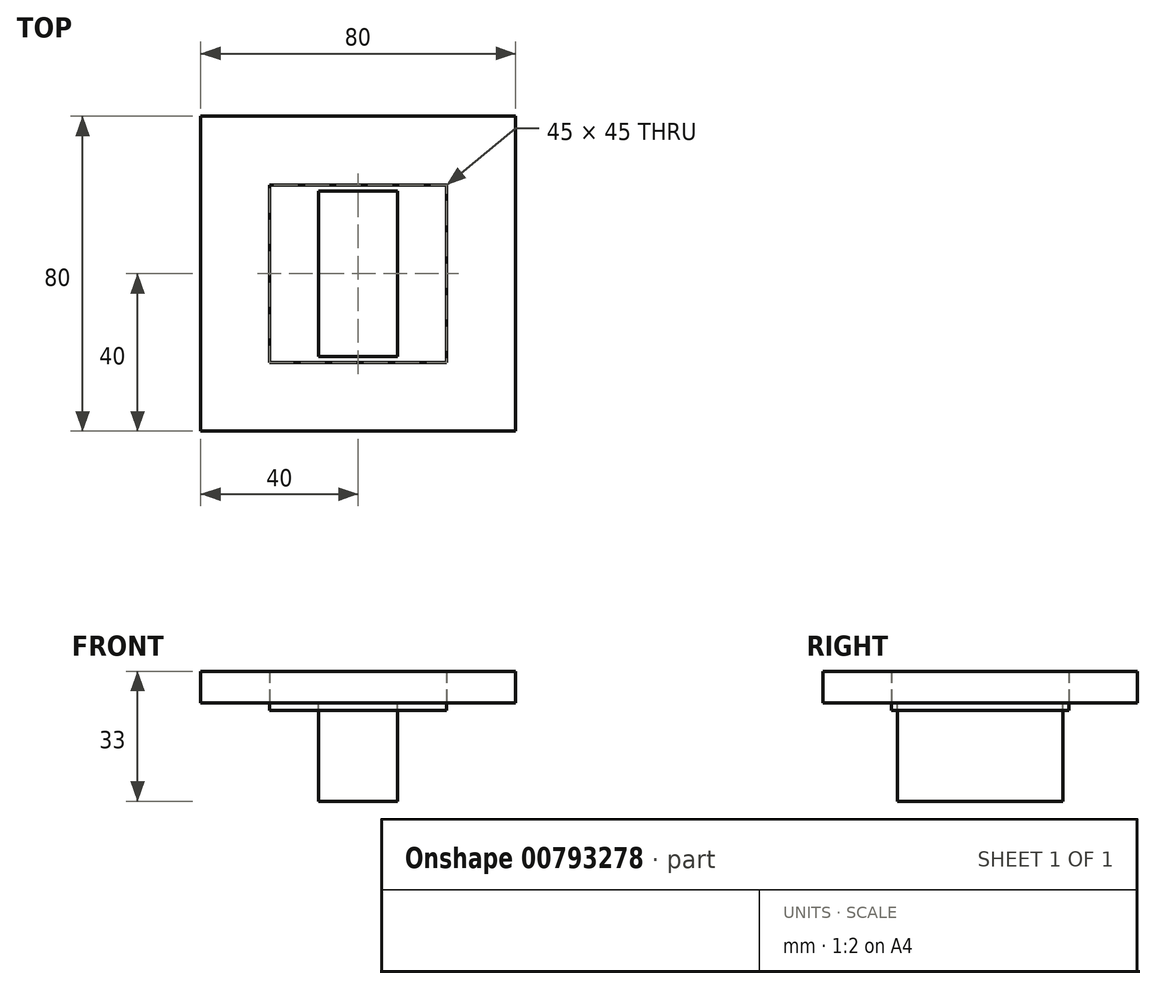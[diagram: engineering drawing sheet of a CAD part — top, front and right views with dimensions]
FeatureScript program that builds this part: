
annotation { "Feature Type Name" : "Feature", "Feature Type Description" : "" }
export const myFeature = defineFeature(function(context is Context, id is Id, definition is map)
    precondition{}
    {
        {
            var Q0;
            Q0=qCreatedBy(makeId("Top.planeOp"),FACE);
            var sketch = newSketch(context, id + "F0", { "sketchPlane" : qUnion([Q0])});
            skLineSegment(sketch, "E0.bottom", {"start": v(40, -40) * mm, "end": v(-40, -40) * mm});
            skLineSegment(sketch, "E0.top", {"start": v(40, 40) * mm, "end": v(-40, 40) * mm});
            skLineSegment(sketch, "E0.left", {"start": v(40, -40) * mm, "end": v(40, 40) * mm});
            skLineSegment(sketch, "E0.right", {"start": v(-40, -40) * mm, "end": v(-40, 40) * mm});
            skPoint(sketch, "E0.middle", {"position": v(0, 0) * mm});
            skLineSegment(sketch, "E1.bottom", {"start": v(22.5, -22.5) * mm, "end": v(-22.5, -22.5) * mm});
            skLineSegment(sketch, "E1.top", {"start": v(22.5, 22.5) * mm, "end": v(-22.5, 22.5) * mm});
            skLineSegment(sketch, "E1.left", {"start": v(22.5, -22.5) * mm, "end": v(22.5, 22.5) * mm});
            skLineSegment(sketch, "E1.right", {"start": v(-22.5, -22.5) * mm, "end": v(-22.5, 22.5) * mm});
            skSolve(sketch);
        }
        {
            var Q0;
            Q0=makeQuery(id+"F0.imprint","IMPRINT",FACE,{"disambiguationData":[TD([[makeQuery(id+"F0.imprint","IMPRINT",EDGE,{"derivedFrom":sQuery(id+"F0.wireOp",EDGE,"E0.bottom")}),-1.0]])]});
            extrude(context, id + "F1", {"entities" : qUnion([Q0]), "depth" : 8 * mm, "offsetDistance" : 25 * mm});
        }
        {
            var Q0;
            Q0=qCreatedBy(makeId("Top.planeOp"),FACE);
            var sketch = newSketch(context, id + "F2", { "sketchPlane" : qUnion([Q0])});
            skLineSegment(sketch, "E2.bottom", {"start": v(10, 21) * mm, "end": v(-10, 21) * mm});
            skLineSegment(sketch, "E2.top", {"start": v(10, -21) * mm, "end": v(-10, -21) * mm});
            skLineSegment(sketch, "E2.left", {"start": v(10, 21) * mm, "end": v(10, -21) * mm});
            skLineSegment(sketch, "E2.right", {"start": v(-10, 21) * mm, "end": v(-10, -21) * mm});
            skPoint(sketch, "E2.middle", {"position": v(0, 0) * mm});
            skSolve(sketch);
        }
        {
            var Q0;
            Q0=makeQuery(id+"F2.imprint","IMPRINT",FACE,{"disambiguationData":[TD([[makeQuery(id+"F2.imprint","IMPRINT",EDGE,{"derivedFrom":sQuery(id+"F2.wireOp",EDGE,"E2.bottom")}),1.0]])]});
            extrude(context, id + "F3", {"entities" : qUnion([Q0]), "oppositeDirection" : true, "depth" : 25 * mm, "offsetDistance" : 25 * mm});
        }
        {
            var Q0;
            Q0=makeQuery(id+"F0.imprint","IMPRINT",FACE,{"disambiguationData":[TD([[makeQuery(id+"F0.imprint","IMPRINT",EDGE,{"derivedFrom":sQuery(id+"F0.wireOp",EDGE,"E1.bottom")}),-1.0]])]});
            extrude(context, id + "F4", {"entities" : qUnion([Q0]), "oppositeDirection" : true, "depth" : 2 * mm, "offsetDistance" : 25 * mm});
        }
    });
